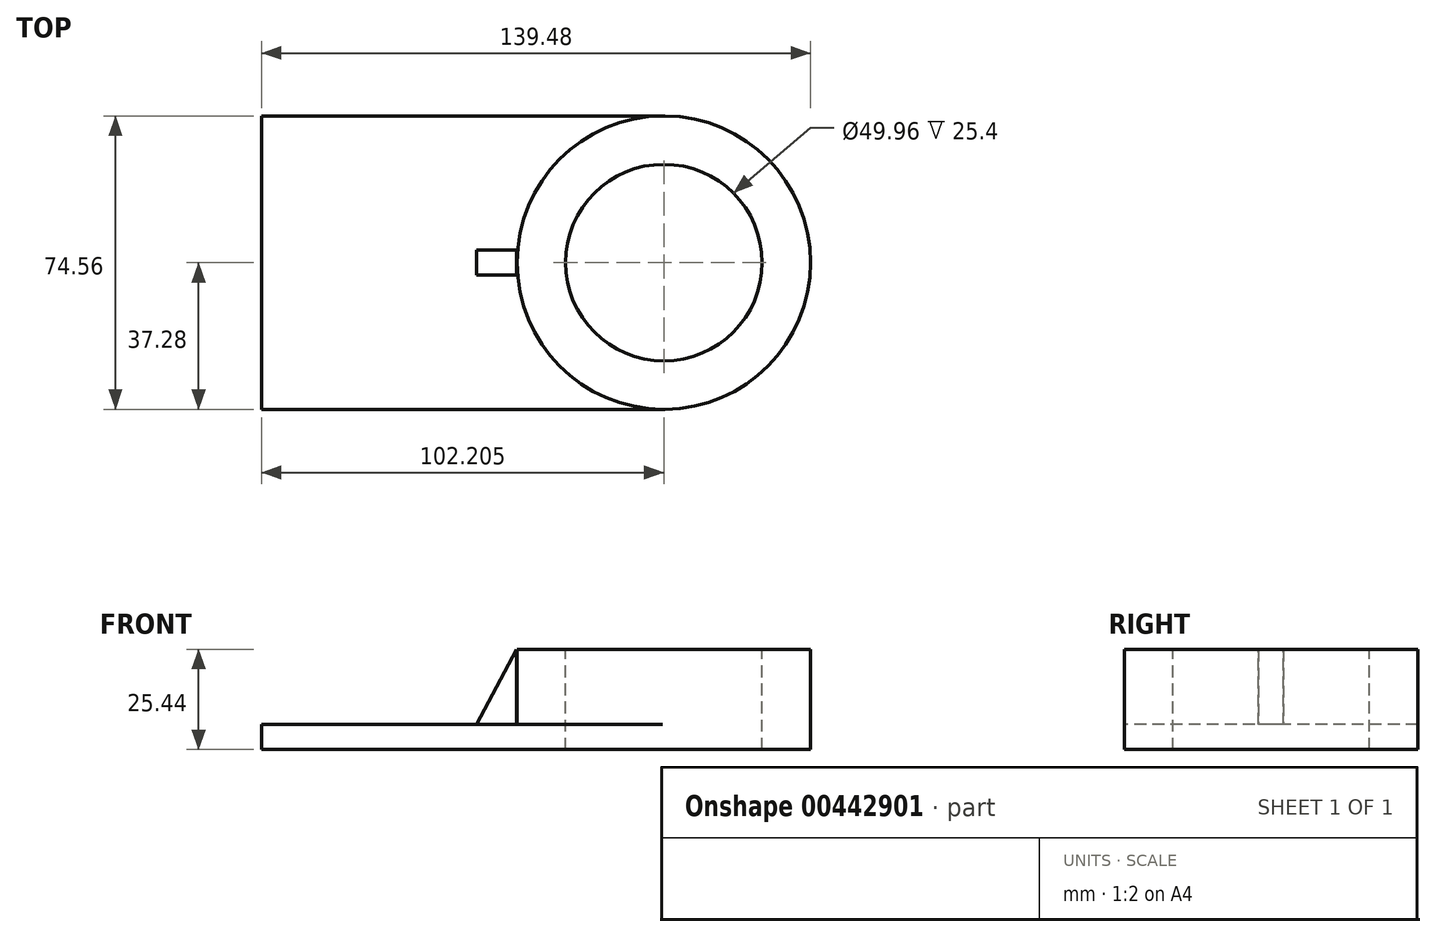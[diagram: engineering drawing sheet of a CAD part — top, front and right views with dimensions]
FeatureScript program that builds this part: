
annotation { "Feature Type Name" : "Feature", "Feature Type Description" : "" }
export const myFeature = defineFeature(function(context is Context, id is Id, definition is map)
    precondition{}
    {
        {
            var Q0;
            Q0=qCreatedBy(makeId("Top.planeOp"),FACE);
            var sketch = newSketch(context, id + "F0", { "sketchPlane" : qUnion([Q0])});
            skLineSegment(sketch, "E0.bottom", {"start": v(-51.24, 37.28) * mm, "end": v(51.24, 37.28) * mm});
            skLineSegment(sketch, "E0.top", {"start": v(-51.24, -37.28) * mm, "end": v(51.24, -37.28) * mm});
            skLineSegment(sketch, "E0.left", {"start": v(-51.24, 37.28) * mm, "end": v(-51.24, -37.28) * mm});
            skLineSegment(sketch, "E0.right", {"start": v(51.24, 37.28) * mm, "end": v(51.24, -37.28) * mm});
            skPoint(sketch, "E0.middle", {"position": v(0, 0) * mm});
            skPoint(sketch, "E1.third.point", {"position": v(86.76, 0) * mm});
            skCircle(sketch, "E2", {"center": v(50.96, 0) * mm, "radius": 37.28 * mm});
            skPoint(sketch, "E2.third.point", {"position": v(88.24, 0) * mm});
            skSolve(sketch);
        }
        {
            var Q0;
            {var subQ1=sQuery(id+"F0.wireOp",EDGE,"E0.right");Q0=makeQuery(id+"F0.imprint","IMPRINT",FACE,{"disambiguationData":[TD([[makeQuery(id+"F0.imprint","IMPRINT",EDGE,{"derivedFrom":subQ1}),-1.0]])]});}
            var Q1;
            {var subQ0=sQuery(id+"F0.wireOp",EDGE,"E0.right");Q1=makeQuery(id+"F0.imprint","IMPRINT",FACE,{"disambiguationData":[TD([[makeQuery(id+"F0.imprint","IMPRINT",EDGE,{"derivedFrom":subQ0}),1.0]])]});}
            extrude(context, id + "F1", {"entities" : qUnion([Q0, Q1]), "depth" : 25.4 * mm});
        }
        {
            var Q0;
            {var subQ0=sQuery(id+"F0.wireOp",EDGE,"E0.left");Q0=makeQuery(id+"F0.imprint","IMPRINT",FACE,{"disambiguationData":[TD([[makeQuery(id+"F0.imprint","IMPRINT",EDGE,{"derivedFrom":subQ0}),1.0]])]});}
            extrude(context, id + "F2", {"entities" : qUnion([Q0]), "operationType" : NewBodyOperationType.ADD, "depth" : 6.35 * mm});
        }
        {
            var Q0;
            Q0=qCreatedBy(makeId("Front.planeOp"),FACE);
            var sketch = newSketch(context, id + "F3", { "sketchPlane" : qUnion([Q0])});
            skLineSegment(sketch, "E3", {"start": v(0, 0) * mm, "end": v(13.6, 25.44) * mm});
            skLineSegment(sketch, "E4", {"start": v(13.6, 25.44) * mm, "end": v(13.6, 0) * mm});
            skLineSegment(sketch, "E5", {"start": v(13.6, 0) * mm, "end": v(0, 0) * mm});
            skSolve(sketch);
        }
        {
            var Q0;
            Q0=makeQuery(id+"F3.imprint","IMPRINT",FACE,{"disambiguationData":[TD([[makeQuery(id+"F3.imprint","IMPRINT",EDGE,{"derivedFrom":sQuery(id+"F3.wireOp",EDGE,"E3")}),-1.0]])]});
            extrude(context, id + "F4", {"entities" : qUnion([Q0]), "operationType" : NewBodyOperationType.ADD, "depth" : 6.35 * mm, "symmetric" : true});
        }
        {
            var Q0;
            Q0=makeQuery(id+"F1.opExtrude","CAP_FACE",FACE,{"disambiguationData":[OSD([sQuery(id+"F0.wireOp",EDGE,"E0.bottom"),sQuery(id+"F0.wireOp",EDGE,"E0.top"),sQuery(id+"F0.wireOp",EDGE,"E2")])],"isStart":false});
            var sketch = newSketch(context, id + "F5", { "sketchPlane" : qUnion([Q0])});
            skCircle(sketch, "E6", {"center": v(50.96, 0) * mm, "radius": 24.98 * mm});
            skSolve(sketch);
        }
        {
            var Q0;
            Q0 = qSketchRegion(id + "F5", true);
            extrude(context, id + "F6", {"entities" : qUnion([Q0]), "operationType" : NewBodyOperationType.REMOVE, "oppositeDirection" : true, "depth" : 89.92 * mm});
        }
    });
